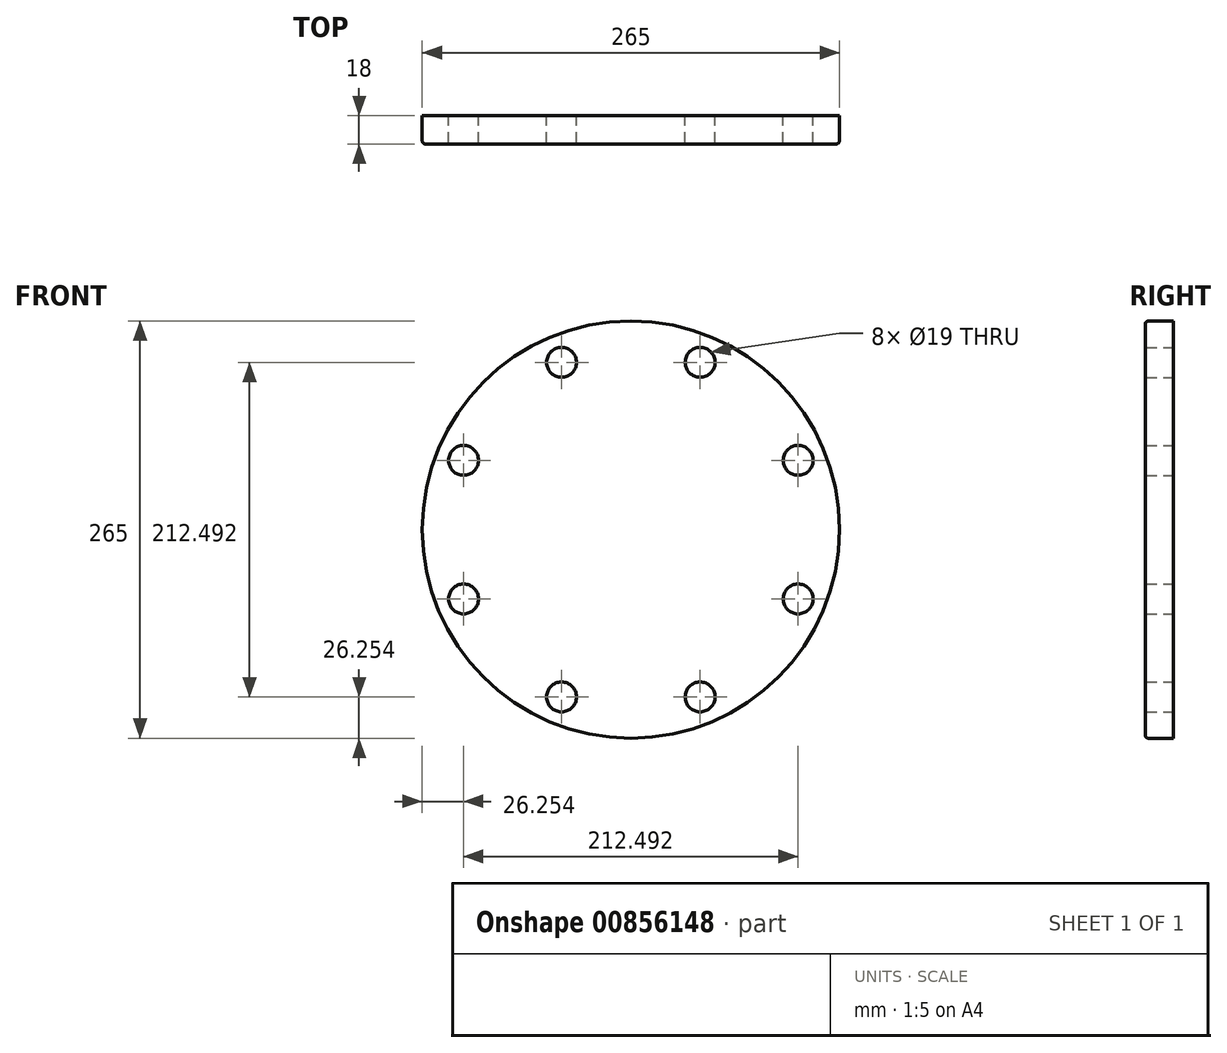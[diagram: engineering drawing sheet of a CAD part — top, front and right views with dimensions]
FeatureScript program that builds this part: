
annotation { "Feature Type Name" : "Feature", "Feature Type Description" : "" }
export const myFeature = defineFeature(function(context is Context, id is Id, definition is map)
    precondition{}
    {
        {
            var Q0;
            Q0=qCreatedBy(makeId("Front.planeOp"),FACE);
            var sketch = newSketch(context, id + "F0", { "sketchPlane" : qUnion([Q0])});
            skLineSegment(sketch, "E0", {"start": v(0, -526.54) * mm, "end": v(0, -90.52) * mm, "construction": true});
            skLineSegment(sketch, "E1", {"start": v(-10.08, -242) * mm, "end": v(258.14, -242) * mm, "construction": true});
            skLineSegment(sketch, "E2.0", {"start": v(-10.08, 0) * mm, "end": v(258.14, 0) * mm, "construction": true});
            skCircle(sketch, "E3", {"center": v(0, 0) * mm, "radius": 132.5 * mm});
            skCircle(sketch, "E4", {"center": v(0, 0) * mm, "radius": 115 * mm, "construction": true});
            skLineSegment(sketch, "E5", {"start": v(32.12, -13.3) * mm, "end": v(0, 0) * mm, "construction": true});
            skCircle(sketch, "E6", {"center": v(106.25, -44) * mm, "radius": 9.5 * mm});
            skCircle(sketch, "E7.1.0", {"center": v(106.25, 44) * mm, "radius": 9.5 * mm});
            skCircle(sketch, "E7.2.0", {"center": v(44, 106.25) * mm, "radius": 9.5 * mm});
            skCircle(sketch, "E7.3.0", {"center": v(-44, 106.25) * mm, "radius": 9.5 * mm});
            skCircle(sketch, "E7.4.0", {"center": v(-106.25, 44) * mm, "radius": 9.5 * mm});
            skCircle(sketch, "E7.5.0", {"center": v(-106.25, -44) * mm, "radius": 9.5 * mm});
            skCircle(sketch, "E7.6.0", {"center": v(-44, -106.25) * mm, "radius": 9.5 * mm});
            skCircle(sketch, "E7.7.0", {"center": v(44, -106.25) * mm, "radius": 9.5 * mm});
            skSolve(sketch);
        }
        {
            var Q0;
            Q0=makeQuery(id+"F0.imprint","IMPRINT",FACE,{"disambiguationData":[TD([[makeQuery(id+"F0.imprint","IMPRINT",EDGE,{"derivedFrom":sQuery(id+"F0.wireOp",EDGE,"E3")}),1.0]])]});
            extrude(context, id + "F1", {"entities" : qUnion([Q0]), "depth" : 18 * mm, "offsetDistance" : 25 * mm});
        }
        {
            var Q0;
            Q0=makeQuery(id+"F1.opExtrude","CAP_EDGE",EDGE,{"disambiguationData":[OSD([sQuery(id+"F0.wireOp",EDGE,"E3")])],"isStart":false});
            fillet(context, id + "F2", {"entities" : qUnion([Q0]), "radius" : 2 * mm, "tangentPropagation" : true, "allowEdgeOverflow" : false});
        }
    });
